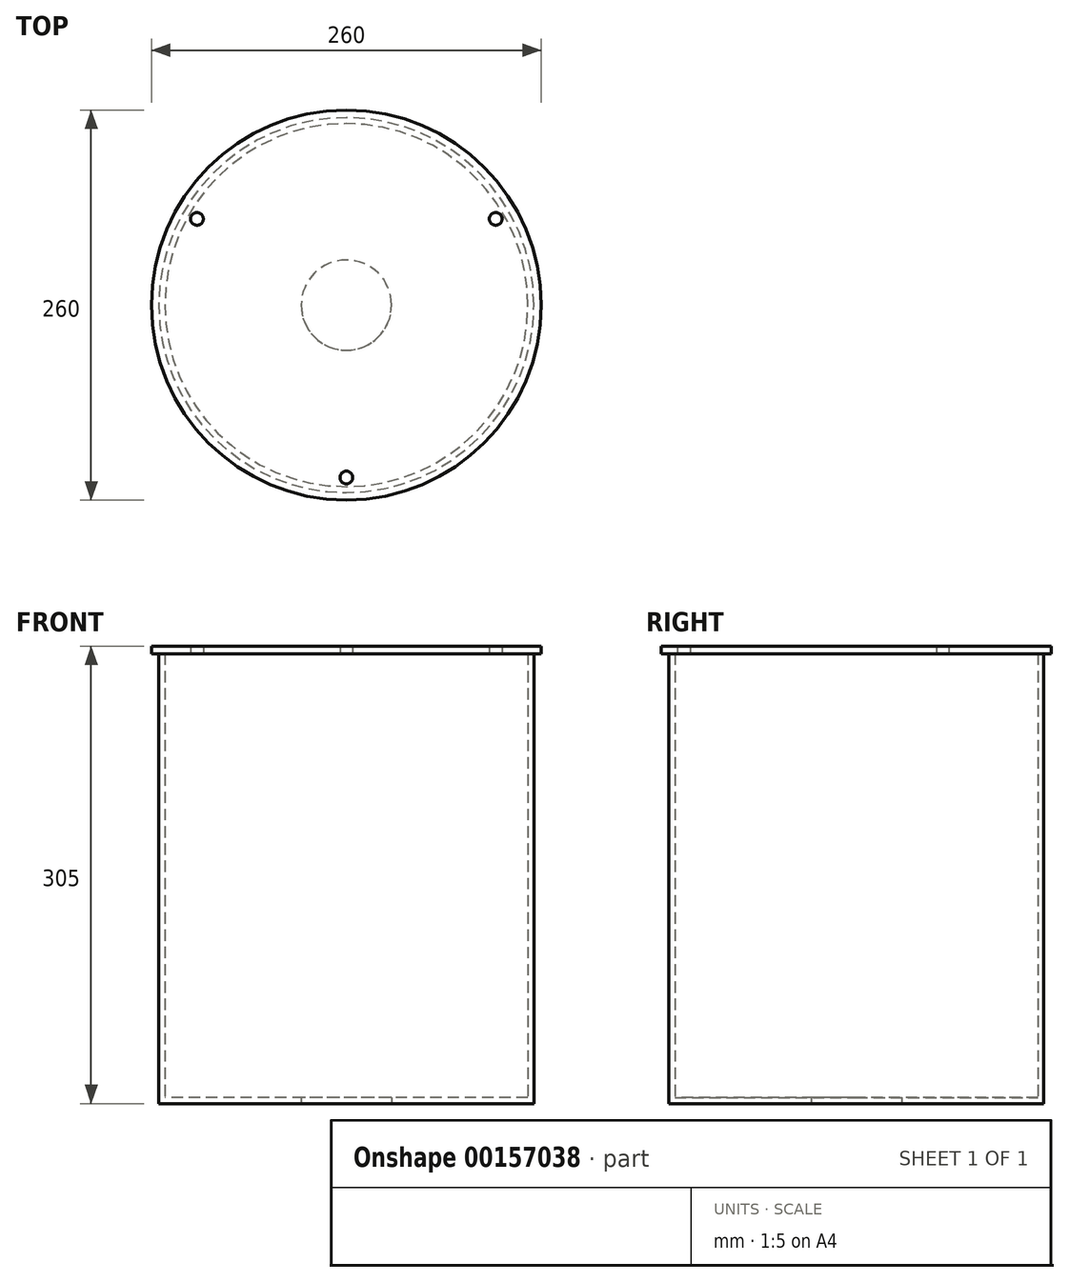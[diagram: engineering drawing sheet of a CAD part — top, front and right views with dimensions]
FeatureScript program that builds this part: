
annotation { "Feature Type Name" : "Feature", "Feature Type Description" : "" }
export const myFeature = defineFeature(function(context is Context, id is Id, definition is map)
    precondition{}
    {
        {
            var Q0;
            Q0=qCreatedBy(makeId("Top.planeOp"),FACE);
            var sketch = newSketch(context, id + "F0", { "sketchPlane" : qUnion([Q0])});
            skCircle(sketch, "E0", {"center": v(0, 0) * mm, "radius": 125 * mm});
            skSolve(sketch);
        }
        {
            var Q0;
            Q0=makeQuery(id+"F0.imprint","IMPRINT",FACE,{"disambiguationData":[TD([[makeQuery(id+"F0.imprint","IMPRINT",EDGE,{"derivedFrom":sQuery(id+"F0.wireOp",EDGE,"E0")}),1.0]])]});
            extrude(context, id + "F1", {"entities" : qUnion([Q0]), "offsetDistance" : 25 * mm, "depth" : 300 * mm});
        }
        {
            var Q0;
            Q0=makeQuery(id+"F1.opExtrude","CAP_FACE",FACE,{"disambiguationData":[OSD([sQuery(id+"F0.wireOp",EDGE,"E0")])],"isStart":false});
            shell(context, id + "F2", {"entities" : qUnion([Q0]), "thickness" : 4 * mm});
        }
        {
            var Q0;
            Q0=makeQuery(id+"F1.opExtrude","CAP_FACE",FACE,{"disambiguationData":[OSD([sQuery(id+"F0.wireOp",EDGE,"E0")])],"isStart":true});
            var sketch = newSketch(context, id + "F3", { "sketchPlane" : qUnion([Q0])});
            skCircle(sketch, "E1", {"center": v(0, 0) * mm, "radius": 30.1 * mm});
            skSolve(sketch);
        }
        {
            var Q0;
            Q0=makeQuery(id+"F3.imprint","IMPRINT",FACE,{"disambiguationData":[TD([[makeQuery(id+"F3.imprint","IMPRINT",EDGE,{"derivedFrom":sQuery(id+"F3.wireOp",EDGE,"E1")}),1.0]])]});
            extrude(context, id + "F4", {"entities" : qUnion([Q0]), "operationType" : NewBodyOperationType.REMOVE, "oppositeDirection" : true, "depth" : 25 * mm});
        }
        {
            var Q0;
            Q0=makeQuery(id+"F1.opExtrude","CAP_FACE",FACE,{"disambiguationData":[OSD([sQuery(id+"F0.wireOp",EDGE,"E0")])],"isStart":false});
            var sketch = newSketch(context, id + "F5", { "sketchPlane" : qUnion([Q0])});
            skCircle(sketch, "E2", {"center": v(0, 0) * mm, "radius": 130 * mm});
            skCircle(sketch, "E3", {"center": v(0, 0) * mm, "radius": 115 * mm, "construction": true});
            skCircle(sketch, "E4", {"center": v(0, -115) * mm, "radius": 4.25 * mm});
            skCircle(sketch, "E5.1.0", {"center": v(99.6, 57.5) * mm, "radius": 4.25 * mm});
            skCircle(sketch, "E5.2.0", {"center": v(-99.6, 57.5) * mm, "radius": 4.25 * mm});
            skSolve(sketch);
        }
        {
            var Q0;
            Q0=makeQuery(id+"F5.imprint","IMPRINT",FACE,{"disambiguationData":[TD([[makeQuery(id+"F5.imprint","IMPRINT",EDGE,{"derivedFrom":sQuery(id+"F5.wireOp",EDGE,"E4")}),-1.0]])]});
            var Q1;
            {var subQ0=sQuery(id+"F0.wireOp",EDGE,"E0");var subQ1=makeQuery(id+"F1.opExtrude","CAP_EDGE",EDGE,{"disambiguationData":[OSD([subQ0])],"isStart":false});Q1=makeQuery(id+"F5.imprint","IMPRINT",FACE,{"disambiguationData":[TD([[makeQuery(id+"F5.imprint","IMPRINT",EDGE,{"derivedFrom":subQ1}),1.0]])]});}
            var Q2;
            Q2=makeQuery(id+"F5.imprint","IMPRINT",FACE,{"disambiguationData":[TD([[makeQuery(id+"F5.imprint","IMPRINT",EDGE,{"derivedFrom":sQuery(id+"F5.wireOp",EDGE,"E2")}),1.0]])]});
            extrude(context, id + "F6", {"entities" : qUnion([Q0, Q1, Q2]), "depth" : 5 * mm});
        }
    });
